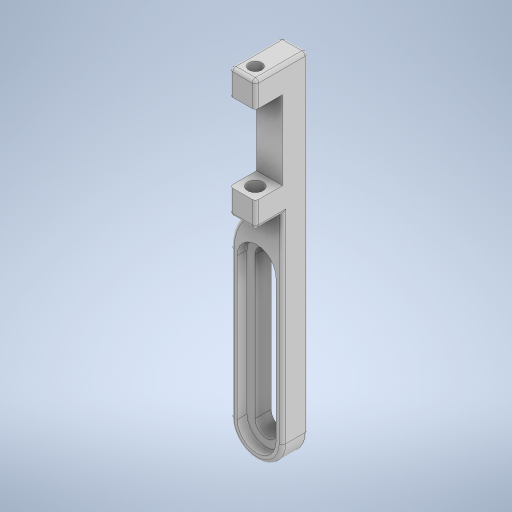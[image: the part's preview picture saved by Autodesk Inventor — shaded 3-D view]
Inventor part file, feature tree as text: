
AUTODESK INVENTOR PART (.ipt)
format: ipt  version: 2024.2 (Build 282272000, 272)  size: 367,616 bytes
history: native  units: mm
features: sketch x6, extrude x5, fillet x4, reference x4, other x2, plane x1
ambient origin geometry x8: Origin, YZ Plane, XZ Plane, XY Plane, X Axis, Y Axis, Z Axis, Center Point
bodies: Solid1 (feature_tree)
feature tree (22):
  plane  "Work Plane1"
  extrude  "Extrusion1"  Depth=4.0mm
  extrude  "Extrusion2"  Depth=30.0mm
  extrude  "Extrusion3"  Depth=4.0mm
  extrude  "Extrusion4"  Depth=4.0mm TaperAngle=0.0deg
  extrude  "Extrusion5"  Depth=1.5mm TaperAngle=0.0deg
  fillet  "Fillet1"  Radius=3.9mm
  fillet  "Fillet2"  Radius=3.9mm
  fillet  "Fillet3"  Radius=4.2mm
  fillet  "Fillet4"  Radius=2.0mm
  sketch  "Sketch6"  dims[d24=2.0mm d25=4.2mm d26=0.0mm d27=2.4mm d28=10.0mm d29=0.0mm d30=1.0mm d31=2.4mm d32=4.0mm d33=8.0mm d34=0.5mm d35=1.0mm d36=20.0mm]
  sketch  "Sketch1"  dims[d4=21.0mm d6=4.0mm]
  reference  "Reference1"
  reference  "Reference2"
  reference  "Reference3"
  reference  "Reference4"
  sketch  "Sketch2"  dims[d7=135.0deg d8=30.0mm]
  sketch  "Sketch3"  dims[d11=4.0mm d12=22.0mm]
  sketch  "Sketch4"  dims[d13=1.75mm d14=4.0mm d15=0.0mm]
  sketch  "Sketch5"  dims[d16=6.0mm d17=1.5mm d18=0.0mm d19=3.9mm d20=3.9mm d21=4.2mm d22=0.0mm d23=2.0mm]
  other  "Assembly1"
  other  "nozzlecleaner:1"
